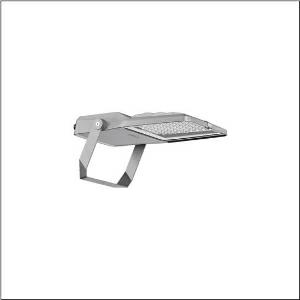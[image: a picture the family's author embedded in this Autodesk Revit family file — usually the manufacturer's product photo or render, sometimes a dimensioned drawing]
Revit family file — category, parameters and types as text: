
# Revit family: floodlight_fl_21_mini___pl61_5xa7776d4c1a_545e
name_source: partatom
category: Lighting Fixtures
units: mm (PartAtom-declared; Revit-internal decimal feet)

## family parameters
Cut with Voids When Loaded = No
Host = Face
Light Source = No
Part Type = Normal
Room Calculation Point = No
Round Connector Dimension = Use Diameter
Shared = No

## types (1)
- --- (1 x LED, 18260 lm, 142.9 W, 4000K)
    Apparent Load = 143 VA
    CIE Flux Codes = 33 65 98 100 100
    Color Rendering = 70
    Color Temperature = 4000K
    Default Elevation = 1800 mm
    Description = Floodlight FL 21 mini, floodlight, primary light control with lens, of PMMA, primary optical cover: protective disc, of toughened safety glass, transparent, light distribution: PL61, light emission: direct distribution, installation type: surface-mounted, LED, High Power LED, rated luminous flux: 18.260lm, luminous efficacy: 128lm/W, light colour: 740, colour temperature: 4000K, control gear: D4iSmart Interface (Zhaga), control: overheat protection, constant luminous flux control, time-dependent luminous flux control, flexible luminous flux parameterisation, pre-setting: logarithmic dimming characteristic, with terminal, 6-pole, mains connection: 220..240V, AC, 50/60Hz, start of lifetime: 143W, end of service life: 151W, reduction: 63W, mounting bracket, of diecast aluminium, powder-coated, SITECO metallic grey (DB 702S), corrosivity category C5 mid according to DIN EN ISO 12944, suitable for swimming pools, chlorine-resistant, sealing non-destructively replaceable, mounting bracket, of steel, galvanised, powder-coated, SITECO metallic grey (DB 702S), Smart Interface below and above, protection rating (complete): IP66, insulation class (complete): insulation class II (safety insulation), certification: CE, ENEC, VDE, protection symbol: D, impact resistance: IK08, permissible operating ambient temperature: -40..+40°C, permissible operating ambient temperature for outdoor applications: -40..+50°C, standard: DIN EN 12944, LABS conformity tested according to VDMA 24364:2018-05, packaging unit: 1 piece

Light Distribution: PL61
    Height = 70 mm
    Lamp = 1 x LED
    Lamp Light Flux = 18260 lm
    Lamp Power = 142.9 W
    Lamp count = 1
    Length = 485 mm
    Luminous efficacy = 128 lm/W
    Manufacturer = Siteco
    ModVariant = No
    Model = 5XA7776D4C1A
    Number of Poles = 1
    OnlyDefault = Yes
    Power Factor = 1
    Product Name = Floodlight FL 21 mini | PL61
    Product group = floodlight | pylon annexe
    ProductGroupID = 6201
    Protection Class = Protection class II
    Protection Degree = IP 66
    RLX_Detail_Level = 1
    RLX_Emergency_Light_Flux = 0 lm
    RLX_Emergency_Type = 0
    RLX_Emergency_Type_DB = No
    RlxData = <blob elided: 96349 chars, md5=06febd2a>
    Socket = socket
    Standby Power = 0 W
    System Light Flux = 18260 lm
    System Power = 143 W
    Type Comments = factory setting: luminous flux: 100 % | dim-lin: 254 | 730 mA
    Type Image = l_1006845.jpg
    URL = http://relux.com
    VarID = @adj_102051
    Voltage = 0 V
    Weight = 0.00 kg
    Width = 337 mm

## geometry (parser evidence)
native form markers: Blend x4, Sweep x11
no freeform markers — native parametric forms only
